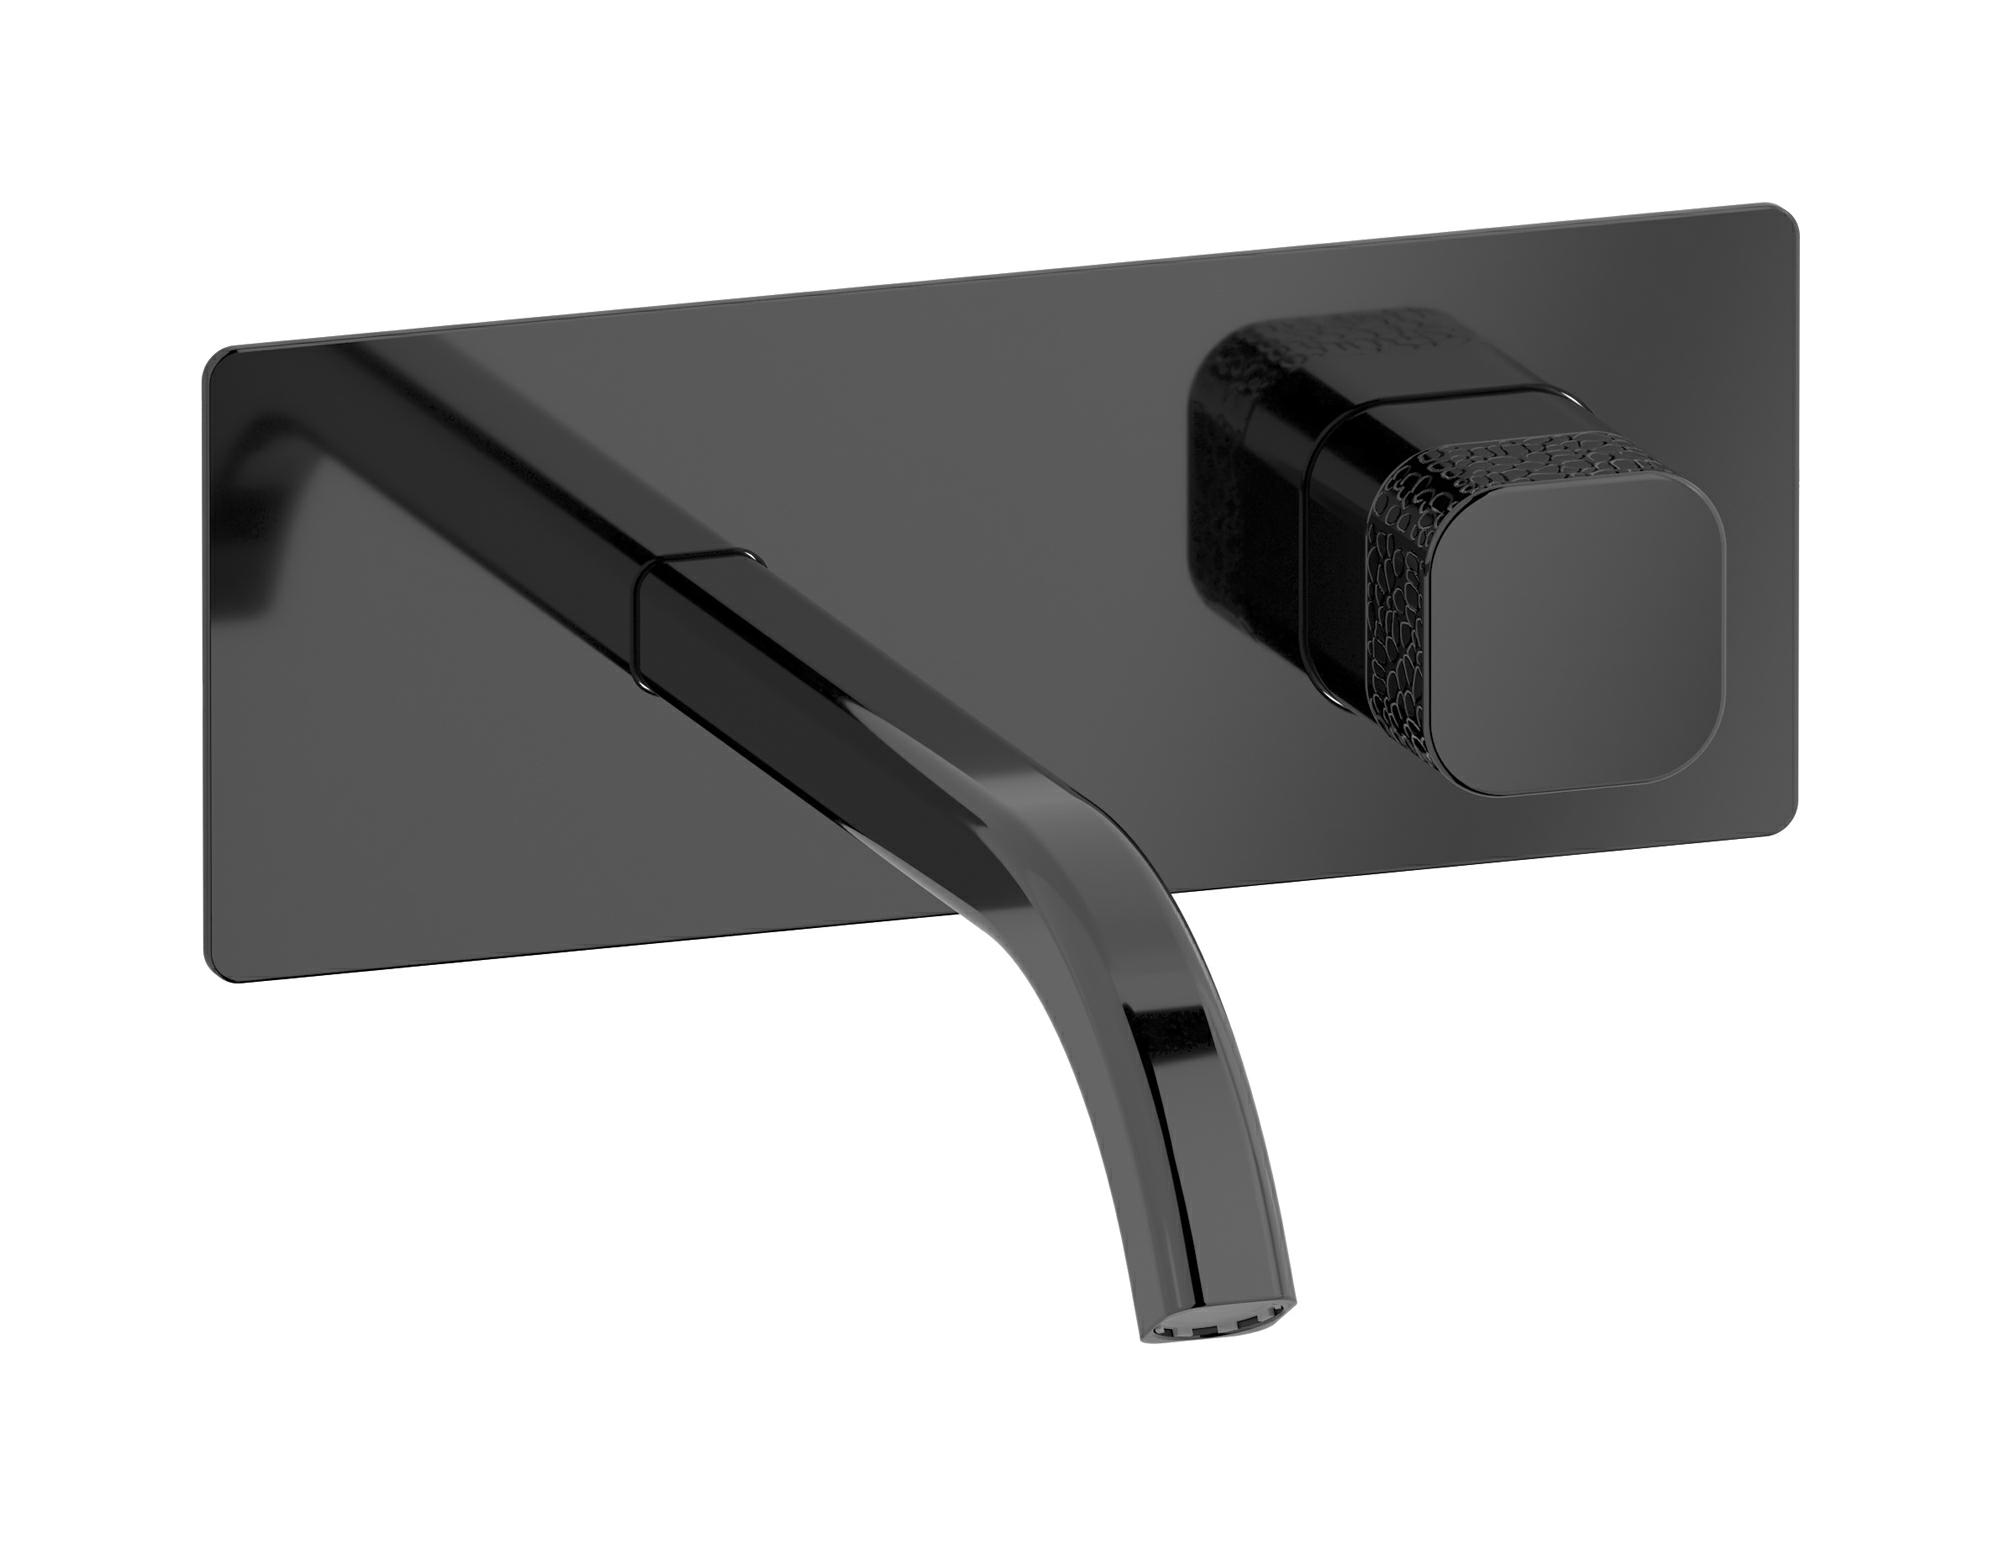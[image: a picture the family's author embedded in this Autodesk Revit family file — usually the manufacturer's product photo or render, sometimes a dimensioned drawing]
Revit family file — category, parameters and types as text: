
# Revit family: EO206_2
name_source: partatom
category: Apparecchi idraulici
units: mm (PartAtom-declared; Revit-internal decimal feet)

## family parameters
Basato su piano di lavoro = No
Condiviso = No
Mantieni orientamento annotazione = No
Numero OmniClass = 23.45.55.17
Punto di calcolo locali = No
Quota connettore circolare = Usa diametro
Sempre verticale = Sì
Taglio con vuoti quando caricato = No
Tipo di parte = Normale
Titolo OmniClass = Mixing Faucets

## types (12) — shared parameters
Cold water inlet = -10 mm  [stored -0.0328084 ft]
Commenti sul tipo = Washbasin
Connessione CW = No
Connessione HW = No
Connessione di scarico = No
Connessione di ventilazione = No
Descrizione = Wall mounted washbasin
Hot water inlet = -10 mm  [stored -0.0328084 ft]
Produttore = IB Rubinetterie S.p.A.
URL = https://www.weareib.it
zero-valued in all types: Prospetto di default

## per-type parameters (varying)
| type | Finishes surface | Immagine tipo | Modello |
| Chrome | IB_Chrome | EO206CC_2.jpg | EO206CC_2 |
| Brushed nickel | IB_Brushed nickel | EO206SS_2.jpg | EO206SS_2 |
| Natural brass | IB_Brass | EO206ON_2.jpg | EO206ON_2 |
| Matt black | IB_matt black | EO206NP_2.jpg | EO206NP_2 |
| Black chrome | IB_Black chrome | EO206CF_2.jpg | EO206CF_2 |
| Brushed black chrome | IB_Brushed black chrome | EO206CS_2.jpg | EO206CS_2 |
| Pale gold | IB_Pale gold | EO206II_2.jpg | EO206II_2 |
| Brushed pale gold | IB_brushed pale gold | EO206IS_2.jpg | EO206IS_2 |
| Rose gold | IB_Rose gold | EO206RS_2.jpg | EO206RS_2 |
| Brushed rose gold | IB_Brushed rose gold | EO206SR_2.jpg | EO206SR_2 |
| Gold | IB_gold | EO206OO_2.jpg | EO206OO_2 |
| Brushed gold | IB_brushed gold | EO206OS_2.jpg | EO206OS_2 |

note: [stored X ft] marks values corroborated as IEEE doubles in the binary element streams (Revit-internal decimal feet)
